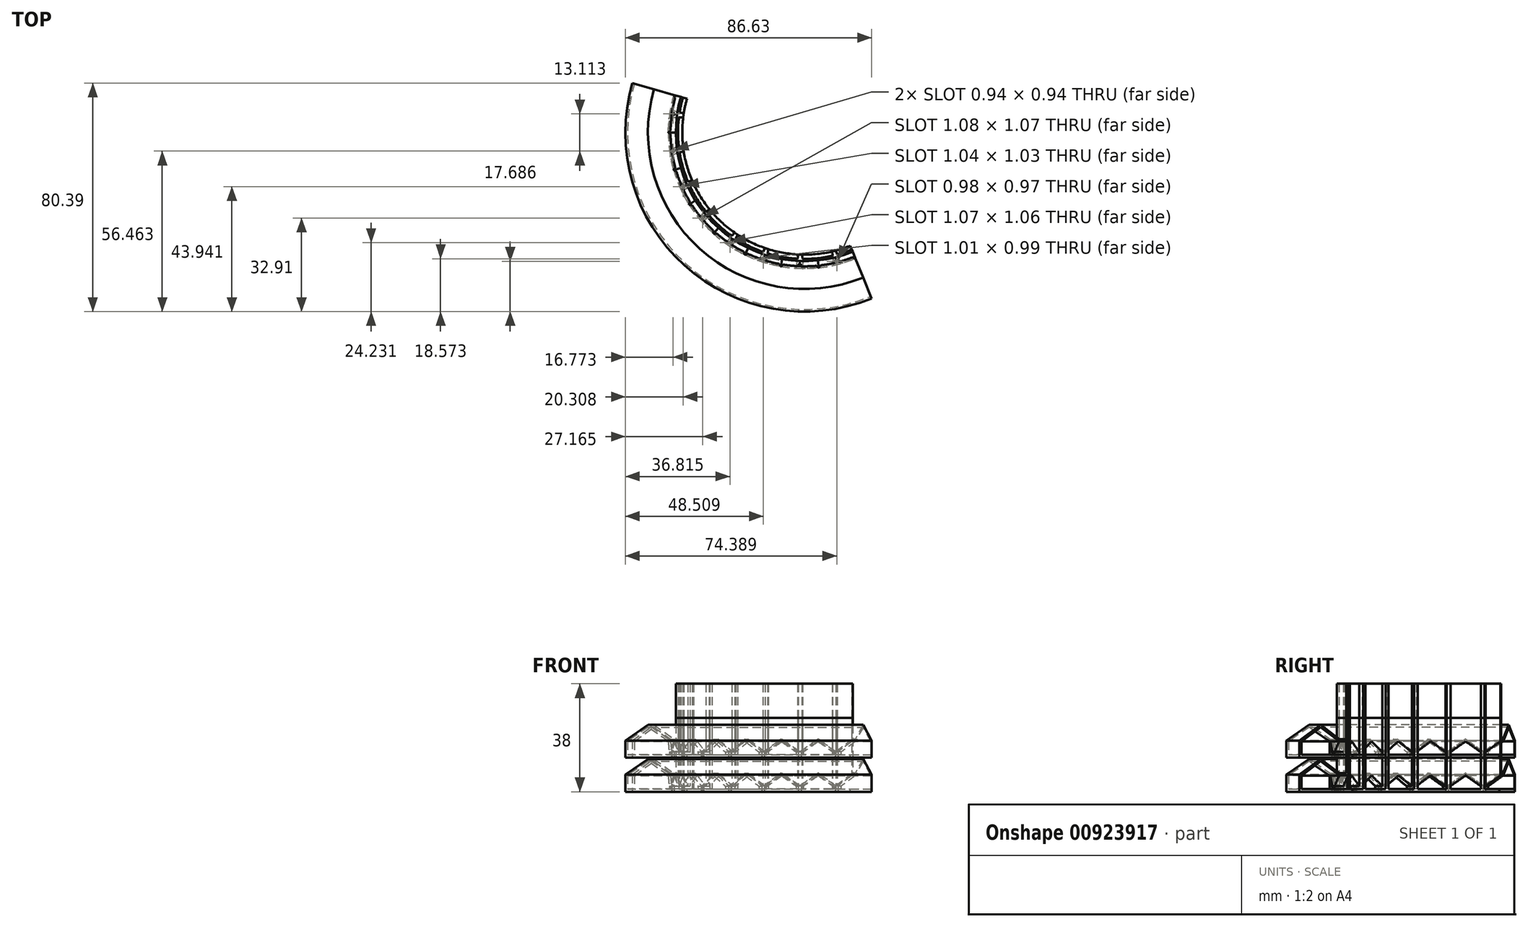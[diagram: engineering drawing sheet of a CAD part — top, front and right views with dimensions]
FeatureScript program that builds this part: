
annotation { "Feature Type Name" : "Feature", "Feature Type Description" : "" }
export const myFeature = defineFeature(function(context is Context, id is Id, definition is map)
    precondition{}
    {
        {
            var Q0;
            Q0=qCreatedBy(makeId("Top.planeOp"),FACE);
            var sketch = newSketch(context, id + "F0", { "sketchPlane" : qUnion([Q0])});
            skLineSegment(sketch, "E0", {"start": v(0, 0) * mm, "end": v(-19.27, 0) * mm});
            skArc(sketch, "E1", {"start": v(0.42, 5.98) * mm, "mid": v(0.1, 3) * mm, "end": v(0, 0) * mm});
            skArc(sketch, "E2", {"start": v(-1.18, 5.34) * mm, "mid": v(-1.42, 2.67) * mm, "end": v(-1.5, 0) * mm});
            skLineSegment(sketch, "E3", {"start": v(0.42, 5.98) * mm, "end": v(-18.67, 8.67) * mm});
            skArc(sketch, "E4", {"start": v(-3.66, 6.56) * mm, "mid": v(-3.69, 6.32) * mm, "end": v(-3.72, 6.09) * mm});
            skArc(sketch, "E5", {"start": v(-18.67, 8.67) * mm, "mid": v(-19.12, 4.34) * mm, "end": v(-19.27, 0) * mm});
            skLineSegment(sketch, "E6", {"start": v(0.33, 5.34) * mm, "end": v(-1.18, 5.34) * mm});
            skArc(sketch, "E7.0", {"start": v(-19.4, 8.77) * mm, "mid": v(-19.87, 4.4) * mm, "end": v(-20.02, 0) * mm});
            skLineSegment(sketch, "E8", {"start": v(-19.4, 8.77) * mm, "end": v(-18.67, 8.67) * mm});
            skLineSegment(sketch, "E9", {"start": v(-20.02, 0) * mm, "end": v(-19.27, 0) * mm});
            skArc(sketch, "E10.0", {"start": v(-4.4, 6.66) * mm, "mid": v(-4.75, 3.34) * mm, "end": v(-4.86, 0) * mm});
            skLineSegment(sketch, "E11", {"start": v(-4.4, 6.66) * mm, "end": v(-3.66, 6.56) * mm});
            skLineSegment(sketch, "E12", {"start": v(-4.86, 0) * mm, "end": v(-4.11, 0) * mm});
            skLineSegment(sketch, "E13", {"start": v(-2.7, 4.3) * mm, "end": v(-2.7, 0) * mm, "construction": true});
            skPoint(sketch, "E13.startSnap0", {"position": v(-2.7, 4.3) * mm});
            skLineSegment(sketch, "E14.0", {"start": v(0.43, 6.09) * mm, "end": v(-3.72, 6.09) * mm});
            skArc(sketch, "E15.trimOffspring", {"start": v(-3.81, 5.34) * mm, "mid": v(-4.04, 2.67) * mm, "end": v(-4.11, 0) * mm});
            skArc(sketch, "E16.0", {"start": v(-1.84, 6.09) * mm, "mid": v(-2.15, 3.05) * mm, "end": v(-2.25, 0) * mm});
            skLineSegment(sketch, "E17.trimOffspring", {"start": v(-1.93, 5.34) * mm, "end": v(-3.81, 5.34) * mm});
            skLineSegment(sketch, "E18", {"start": v(-3.81, 5.34) * mm, "end": v(-3.72, 6.09) * mm});
            skPoint(sketch, "E19", {"position": v(-0.32, 6.09) * mm});
            skSolve(sketch);
        }
        {
            var Q0;
            {var subQ8=sQuery(id+"F0.wireOp",EDGE,"E2");Q0=makeQuery(id+"F0.imprint","IMPRINT",FACE,{"disambiguationData":[TD([[makeQuery(id+"F0.imprint","IMPRINT",EDGE,{"derivedFrom":subQ8}),-1.0]])]});}
            extrude(context, id + "F1", {"entities" : qUnion([Q0]), "depth" : 25 * mm, "offsetDistance" : 25 * mm});
        }
        {
            var Q0;
            Q0=qCreatedBy(makeId("Right.planeOp"),FACE);
            var Q1;
            Q1=sQuery(id+"F0.wireOp",VERTEX,"E13.end");
            cPlane(context, id + "F2", {"entities" : qUnion([Q0, Q1]), "cplaneType" : CPlaneType.PLANE_POINT, "offset" : 25 * mm, "width" : 150 * mm, "height" : 150 * mm});
        }
        {
            var Q0;
            Q0=qCreatedBy(id+"F2.planeOp",FACE);
            var sketch = newSketch(context, id + "F3", { "sketchPlane" : qUnion([Q0])});
            skLineSegment(sketch, "E20.bottom", {"start": v(0, 0) * mm, "end": v(6.09, 0) * mm});
            skLineSegment(sketch, "E20.left", {"start": v(0, 0) * mm, "end": v(0, 0) * mm});
            skLineSegment(sketch, "E20.right", {"start": v(6.09, 0) * mm, "end": v(6.09, 1.28) * mm});
            skLineSegment(sketch, "E21", {"start": v(0, 0) * mm, "end": v(0, 5.54) * mm});
            skLineSegment(sketch, "E22", {"start": v(0, 5.54) * mm, "end": v(6.09, 1.28) * mm});
            skLineSegment(sketch, "E23", {"start": v(0, 4.74) * mm, "end": v(5.34, 1) * mm});
            skLineSegment(sketch, "E24", {"start": v(5.34, 1) * mm, "end": v(5.34, 0) * mm});
            skLineSegment(sketch, "E25", {"start": v(2.67, 2.87) * mm, "end": v(3.82, 2.87) * mm, "construction": true});
            skSolve(sketch);
        }
        {
            var Q0;
            Q0=makeQuery(id+"F0.imprint","IMPRINT",FACE,{"disambiguationData":[TD([[makeQuery(id+"F0.imprint","IMPRINT",EDGE,{"derivedFrom":sQuery(id+"F0.wireOp",EDGE,"E5")}),-1.0]])]});
            var Q1;
            {var subQ0=sQuery(id+"F0.wireOp",EDGE,"E4");Q1=makeQuery(id+"F0.imprint","IMPRINT",FACE,{"disambiguationData":[TD([[makeQuery(id+"F0.imprint","IMPRINT",EDGE,{"derivedFrom":subQ0}),-1.0]])]});}
            extrude(context, id + "F4", {"entities" : qUnion([Q0, Q1]), "depth" : 5 * mm, "offsetDistance" : 25 * mm});
        }
        {
            var Q0;
            Q0=qCreatedBy(makeId("Front.planeOp"),FACE);
            var sketch = newSketch(context, id + "F5", { "sketchPlane" : qUnion([Q0])});
            skLineSegment(sketch, "E26", {"start": v(-20.02, 5) * mm, "end": v(-12.07, 10.57) * mm});
            skLineSegment(sketch, "E27", {"start": v(-12.07, 10.57) * mm, "end": v(-4.11, 5) * mm});
            skLineSegment(sketch, "E28", {"start": v(-4.11, 5) * mm, "end": v(-20.02, 5) * mm, "construction": true});
            skLineSegment(sketch, "E29", {"start": v(-19.27, 4.68) * mm, "end": v(-12.07, 9.73) * mm});
            skLineSegment(sketch, "E30", {"start": v(-12.07, 9.73) * mm, "end": v(-4.86, 4.68) * mm});
            skLineSegment(sketch, "E31", {"start": v(-12.07, 9.73) * mm, "end": v(-12.07, 10.57) * mm, "construction": true});
            skLineSegment(sketch, "E32", {"start": v(-18.9, 5.78) * mm, "end": v(-17.7, 5.78) * mm});
            skPoint(sketch, "E33", {"position": v(-12.07, 5) * mm});
            skLineSegment(sketch, "E34", {"start": v(-19.27, 4.68) * mm, "end": v(-20.02, 5) * mm});
            skLineSegment(sketch, "E35", {"start": v(-4.86, 4.68) * mm, "end": v(-4.11, 5) * mm});
            skLineSegment(sketch, "E36", {"start": v(43, 0) * mm, "end": v(43, 30.19) * mm});
            skSolve(sketch);
        }
        {
            var Q0;
            {var subQ2=sQuery(id+"F5.wireOp",EDGE,"E32");Q0=makeQuery(id+"F5.imprint","IMPRINT",FACE,{"disambiguationData":[TD([[makeQuery(id+"F5.imprint","IMPRINT",EDGE,{"derivedFrom":subQ2}),-1.0]])]});}
            var Q1;
            {var subQ3=sQuery(id+"F5.wireOp",EDGE,"E27");Q1=makeQuery(id+"F5.imprint","IMPRINT",FACE,{"disambiguationData":[TD([[makeQuery(id+"F5.imprint","IMPRINT",EDGE,{"derivedFrom":subQ3}),-1.0]])]});}
            var Q2;
            Q2=sQuery(id+"F5.wireOp",EDGE,"E36");
            revolve(context, id + "F6", {"operationType" : NewBodyOperationType.ADD, "surfaceOperationType" : NewSurfaceOperationType.NEW, "entities" : qUnion([Q0, Q1]), "axis" : qUnion([Q2]), "revolveType" : RevolveType.ONE_DIRECTION, "oppositeDirection" : true, "angle" : 8 * degree});
        }
        {
            var Q0;
            {var subQ3=sQuery(id+"F3.wireOp",EDGE,"E20.right");Q0=makeQuery(id+"F3.imprint","IMPRINT",FACE,{"disambiguationData":[TD([[makeQuery(id+"F3.imprint","IMPRINT",EDGE,{"derivedFrom":subQ3}),1.0]])]});}
            var Q1;
            Q1=makeQuery(id+"F4.opExtrude","SWEPT_BODY",BODY,{"disambiguationData":[OSD([sQuery(id+"F0.wireOp",EDGE,"E0"),sQuery(id+"F0.wireOp",EDGE,"E3"),sQuery(id+"F0.wireOp",EDGE,"E4"),sQuery(id+"F0.wireOp",EDGE,"E10.0"),sQuery(id+"F0.wireOp",EDGE,"E15.trimOffspring"),sQuery(id+"F0.wireOp",EDGE,"E18")])]});
            var Q2;
            Q2=makeQuery(id+"F1.opExtrude","SWEPT_BODY",BODY,{"disambiguationData":[OSD([sQuery(id+"F0.wireOp",EDGE,"E0"),sQuery(id+"F0.wireOp",EDGE,"E1"),sQuery(id+"F0.wireOp",EDGE,"E2"),sQuery(id+"F0.wireOp",EDGE,"E3"),sQuery(id+"F0.wireOp",EDGE,"E6"),sQuery(id+"F0.wireOp",EDGE,"E14.0"),sQuery(id+"F0.wireOp",EDGE,"E16.0")])]});
            extrude(context, id + "F7", {"entities" : qUnion([Q0]), "operationType" : NewBodyOperationType.ADD, "endBound" : BoundingType.UP_TO_BODY, "oppositeDirection" : true, "depth" : 25 * mm, "endBoundEntityBody" : qUnion([Q1]), "offsetDistance" : 25 * mm, "hasSecondDirection" : true, "secondDirectionBound" : SecondDirectionBoundingType.UP_TO_BODY, "secondDirectionOppositeDirection" : false, "secondDirectionDepth" : 25 * mm, "secondDirectionBoundEntityBody" : qUnion([Q2])});
        }
        {
            var Q0;
            {var subQ4=sQuery(id+"F3.wireOp",EDGE,"E23");Q0=makeQuery(id+"F3.imprint","IMPRINT",FACE,{"disambiguationData":[TD([[makeQuery(id+"F3.imprint","IMPRINT",EDGE,{"derivedFrom":subQ4}),-1.0]])]});}
            extrude(context, id + "F8", {"entities" : qUnion([Q0]), "operationType" : NewBodyOperationType.REMOVE, "endBound" : BoundingType.SYMMETRIC, "oppositeDirection" : true, "depth" : 10 * mm, "offsetDistance" : 25 * mm});
        }
        {
            var Q0;
            {var subQ3=sQuery(id+"F0.wireOp",EDGE,"E2");Q0=makeQuery(id+"F0.imprint","IMPRINT",FACE,{"disambiguationData":[TD([[makeQuery(id+"F0.imprint","IMPRINT",EDGE,{"derivedFrom":subQ3}),1.0]])]});}
            var Q1;
            {var subQ8=sQuery(id+"F0.wireOp",EDGE,"E2");Q1=makeQuery(id+"F0.imprint","IMPRINT",FACE,{"disambiguationData":[TD([[makeQuery(id+"F0.imprint","IMPRINT",EDGE,{"derivedFrom":subQ8}),-1.0]])]});}
            var Q2;
            {var subQ3=sQuery(id+"F0.wireOp",EDGE,"E15.trimOffspring");Q2=makeQuery(id+"F0.imprint","IMPRINT",FACE,{"disambiguationData":[TD([[makeQuery(id+"F0.imprint","IMPRINT",EDGE,{"derivedFrom":subQ3}),1.0]])]});}
            var Q3;
            {var subQ4=sQuery(id+"F0.wireOp",EDGE,"E17.trimOffspring");Q3=makeQuery(id+"F0.imprint","IMPRINT",FACE,{"disambiguationData":[TD([[makeQuery(id+"F0.imprint","IMPRINT",EDGE,{"derivedFrom":subQ4}),-1.0]])]});}
            var Q4;
            {var subQ0=sQuery(id+"F0.wireOp",EDGE,"E4");Q4=makeQuery(id+"F0.imprint","IMPRINT",FACE,{"disambiguationData":[TD([[makeQuery(id+"F0.imprint","IMPRINT",EDGE,{"derivedFrom":subQ0}),-1.0]])]});}
            var Q5;
            {var subQ2=sQuery(id+"F0.wireOp",EDGE,"E5");Q5=makeQuery(id+"F0.imprint","IMPRINT",FACE,{"disambiguationData":[TD([[makeQuery(id+"F0.imprint","IMPRINT",EDGE,{"derivedFrom":subQ2}),1.0]])]});}
            var Q6;
            Q6=makeQuery(id+"F0.imprint","IMPRINT",FACE,{"disambiguationData":[TD([[makeQuery(id+"F0.imprint","IMPRINT",EDGE,{"derivedFrom":sQuery(id+"F0.wireOp",EDGE,"E5")}),-1.0]])]});
            extrude(context, id + "F9", {"entities" : qUnion([Q0, Q1, Q2, Q3, Q4, Q5, Q6]), "operationType" : NewBodyOperationType.ADD, "oppositeDirection" : true, "depth" : 1 * mm, "offsetDistance" : 25 * mm});
        }
        {
            var Q0;
            Q0=makeQuery(id+"F1.opExtrude","SWEPT_BODY",BODY,{"disambiguationData":[OSD([sQuery(id+"F0.wireOp",EDGE,"E0"),sQuery(id+"F0.wireOp",EDGE,"E1"),sQuery(id+"F0.wireOp",EDGE,"E2"),sQuery(id+"F0.wireOp",EDGE,"E3"),sQuery(id+"F0.wireOp",EDGE,"E6"),sQuery(id+"F0.wireOp",EDGE,"E14.0"),sQuery(id+"F0.wireOp",EDGE,"E16.0")])]});
            var Q1;
            {var subQ0=sQuery(id+"F0.wireOp",EDGE,"E3");Q1=makeQuery(id+"F9.boolean.opBoolean","MERGE",FACE,{"derivedFrom":[makeQuery(id+"F1.opExtrude","SWEPT_FACE",FACE,{"disambiguationData":[OSD([subQ0])]}),makeQuery(id+"F9.opExtrude","SWEPT_FACE",FACE,{"disambiguationData":[OSD([subQ0])]})]});}
            mirror(context, id + "F10", {"operationType" : NewBodyOperationType.ADD, "entities" : qUnion([Q0]), "mirrorPlane" : qUnion([Q1])});
        }
        {
            var Q0;
            {var subQ0=sQuery(id+"F0.wireOp",EDGE,"E14.0");var subQ1=sQuery(id+"F0.wireOp",EDGE,"E3");var subQ2=makeQuery(id+"F9.boolean.opBoolean","MERGE",EDGE,{"derivedFrom":[makeQuery(id+"F1.opExtrude","SWEPT_EDGE",EDGE,{"disambiguationData":[OSD([subQ1,subQ0])]}),makeQuery(id+"F9.opExtrude","SWEPT_EDGE",EDGE,{"disambiguationData":[OSD([subQ1,subQ0])]})]});Q0=makeQuery(id+"F10.boolean.opBoolean","MERGE",EDGE,{"derivedFrom":[subQ2,makeQuery(id+"F10.opPattern","COPY",EDGE,{"derivedFrom":subQ2,"instanceName":"1"})]});}
            fillet(context, id + "F11", {"entities" : qUnion([Q0]), "radius" : 0.4 * mm, "tangentPropagation" : true, "allowEdgeOverflow" : false});
        }
        {
            var Q0;
            Q0=makeQuery(id+"F1.opExtrude","SWEPT_BODY",BODY,{"disambiguationData":[OSD([sQuery(id+"F0.wireOp",EDGE,"E0"),sQuery(id+"F0.wireOp",EDGE,"E1"),sQuery(id+"F0.wireOp",EDGE,"E2"),sQuery(id+"F0.wireOp",EDGE,"E3"),sQuery(id+"F0.wireOp",EDGE,"E6"),sQuery(id+"F0.wireOp",EDGE,"E14.0"),sQuery(id+"F0.wireOp",EDGE,"E16.0")])]});
            var Q1;
            {var subQ0=sQuery(id+"F0.wireOp",EDGE,"E9");var subQ1=sQuery(id+"F0.wireOp",EDGE,"E0");Q1=makeQuery(id+"F9.boolean.opBoolean","MERGE",FACE,{"derivedFrom":[makeQuery(id+"F7.boolean.opBoolean","MERGE",FACE,{"derivedFrom":[makeQuery(id+"F1.opExtrude","SWEPT_FACE",FACE,{"disambiguationData":[OSD([subQ1])]}),makeQuery(id+"F6.boolean.opBoolean","MERGE",FACE,{"derivedFrom":[makeQuery(id+"F4.opExtrude","SWEPT_FACE",FACE,{"disambiguationData":[OSD([subQ1])]}),makeQuery(id+"F4.opExtrude","SWEPT_FACE",FACE,{"disambiguationData":[OSD([subQ0])]}),makeQuery(id+"F6.opRevolve","CAP_FACE",FACE,{"disambiguationData":[OSD([sQuery(id+"F5.wireOp",EDGE,"E26"),sQuery(id+"F5.wireOp",EDGE,"E27"),sQuery(id+"F5.wireOp",EDGE,"E29"),sQuery(id+"F5.wireOp",EDGE,"E30"),sQuery(id+"F5.wireOp",EDGE,"E34"),sQuery(id+"F5.wireOp",EDGE,"E35")])],"isStart":true})]}),makeQuery(id+"F7.opExtrude","SWEPT_FACE",FACE,{"disambiguationData":[OSD([sQuery(id+"F3.wireOp",EDGE,"E21")])]})]}),makeQuery(id+"F9.opExtrude","SWEPT_FACE",FACE,{"disambiguationData":[OSD([subQ1,subQ0])]})]});}
            mirror(context, id + "F12", {"operationType" : NewBodyOperationType.ADD, "entities" : qUnion([Q0]), "mirrorPlane" : qUnion([Q1])});
        }
        {
            var Q0;
            Q0=makeQuery(id+"F1.opExtrude","SWEPT_BODY",BODY,{"disambiguationData":[OSD([sQuery(id+"F0.wireOp",EDGE,"E0"),sQuery(id+"F0.wireOp",EDGE,"E1"),sQuery(id+"F0.wireOp",EDGE,"E2"),sQuery(id+"F0.wireOp",EDGE,"E3"),sQuery(id+"F0.wireOp",EDGE,"E6"),sQuery(id+"F0.wireOp",EDGE,"E14.0"),sQuery(id+"F0.wireOp",EDGE,"E16.0")])]});
            var Q1;
            {var subQ0=sQuery(id+"F0.wireOp",EDGE,"E9");var subQ1=sQuery(id+"F0.wireOp",EDGE,"E0");Q1=makeQuery(id+"F12.opPattern","COPY",FACE,{"derivedFrom":makeQuery(id+"F10.opPattern","COPY",FACE,{"derivedFrom":makeQuery(id+"F9.boolean.opBoolean","MERGE",FACE,{"derivedFrom":[makeQuery(id+"F7.boolean.opBoolean","MERGE",FACE,{"derivedFrom":[makeQuery(id+"F1.opExtrude","SWEPT_FACE",FACE,{"disambiguationData":[OSD([subQ1])]}),makeQuery(id+"F6.boolean.opBoolean","MERGE",FACE,{"derivedFrom":[makeQuery(id+"F4.opExtrude","SWEPT_FACE",FACE,{"disambiguationData":[OSD([subQ1])]}),makeQuery(id+"F4.opExtrude","SWEPT_FACE",FACE,{"disambiguationData":[OSD([subQ0])]}),makeQuery(id+"F6.opRevolve","CAP_FACE",FACE,{"disambiguationData":[OSD([sQuery(id+"F5.wireOp",EDGE,"E26"),sQuery(id+"F5.wireOp",EDGE,"E27"),sQuery(id+"F5.wireOp",EDGE,"E29"),sQuery(id+"F5.wireOp",EDGE,"E30"),sQuery(id+"F5.wireOp",EDGE,"E34"),sQuery(id+"F5.wireOp",EDGE,"E35")])],"isStart":true})]}),makeQuery(id+"F7.opExtrude","SWEPT_FACE",FACE,{"disambiguationData":[OSD([sQuery(id+"F3.wireOp",EDGE,"E21")])]})]}),makeQuery(id+"F9.opExtrude","SWEPT_FACE",FACE,{"disambiguationData":[OSD([subQ1,subQ0])]})]}),"instanceName":"1"}),"instanceName":"1"});}
            mirror(context, id + "F13", {"operationType" : NewBodyOperationType.ADD, "entities" : qUnion([Q0]), "mirrorPlane" : qUnion([Q1])});
        }
        {
            var Q0;
            Q0=makeQuery(id+"F1.opExtrude","SWEPT_BODY",BODY,{"disambiguationData":[OSD([sQuery(id+"F0.wireOp",EDGE,"E0"),sQuery(id+"F0.wireOp",EDGE,"E1"),sQuery(id+"F0.wireOp",EDGE,"E2"),sQuery(id+"F0.wireOp",EDGE,"E3"),sQuery(id+"F0.wireOp",EDGE,"E6"),sQuery(id+"F0.wireOp",EDGE,"E14.0"),sQuery(id+"F0.wireOp",EDGE,"E16.0")])]});
            var Q1;
            {var subQ0=sQuery(id+"F0.wireOp",EDGE,"E9");var subQ1=sQuery(id+"F0.wireOp",EDGE,"E0");Q1=makeQuery(id+"F13.opPattern","COPY",FACE,{"derivedFrom":makeQuery(id+"F10.opPattern","COPY",FACE,{"derivedFrom":makeQuery(id+"F9.boolean.opBoolean","MERGE",FACE,{"derivedFrom":[makeQuery(id+"F7.boolean.opBoolean","MERGE",FACE,{"derivedFrom":[makeQuery(id+"F1.opExtrude","SWEPT_FACE",FACE,{"disambiguationData":[OSD([subQ1])]}),makeQuery(id+"F6.boolean.opBoolean","MERGE",FACE,{"derivedFrom":[makeQuery(id+"F4.opExtrude","SWEPT_FACE",FACE,{"disambiguationData":[OSD([subQ1])]}),makeQuery(id+"F4.opExtrude","SWEPT_FACE",FACE,{"disambiguationData":[OSD([subQ0])]}),makeQuery(id+"F6.opRevolve","CAP_FACE",FACE,{"disambiguationData":[OSD([sQuery(id+"F5.wireOp",EDGE,"E26"),sQuery(id+"F5.wireOp",EDGE,"E27"),sQuery(id+"F5.wireOp",EDGE,"E29"),sQuery(id+"F5.wireOp",EDGE,"E30"),sQuery(id+"F5.wireOp",EDGE,"E34"),sQuery(id+"F5.wireOp",EDGE,"E35")])],"isStart":true})]}),makeQuery(id+"F7.opExtrude","SWEPT_FACE",FACE,{"disambiguationData":[OSD([sQuery(id+"F3.wireOp",EDGE,"E21")])]})]}),makeQuery(id+"F9.opExtrude","SWEPT_FACE",FACE,{"disambiguationData":[OSD([subQ1,subQ0])]})]}),"instanceName":"1"}),"instanceName":"1"});}
            mirror(context, id + "F14", {"operationType" : NewBodyOperationType.ADD, "entities" : qUnion([Q0]), "mirrorPlane" : qUnion([Q1])});
        }
        {
            var Q0;
            Q0=makeQuery(id+"F1.opExtrude","SWEPT_BODY",BODY,{"disambiguationData":[OSD([sQuery(id+"F0.wireOp",EDGE,"E0"),sQuery(id+"F0.wireOp",EDGE,"E1"),sQuery(id+"F0.wireOp",EDGE,"E2"),sQuery(id+"F0.wireOp",EDGE,"E3"),sQuery(id+"F0.wireOp",EDGE,"E6"),sQuery(id+"F0.wireOp",EDGE,"E14.0"),sQuery(id+"F0.wireOp",EDGE,"E16.0")])]});
            var Q1;
            Q1=sQuery(id+"F5.wireOp",EDGE,"E36");
            transform(context, id + "F15", {"entities" : qUnion([Q0]), "transformType" : TransformType.TRANSLATION_DISTANCE, "transformDirection" : qUnion([Q1]), "distance" : 12 * mm, "makeCopy" : true});
        }
    });
